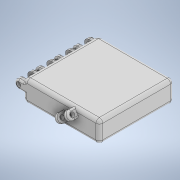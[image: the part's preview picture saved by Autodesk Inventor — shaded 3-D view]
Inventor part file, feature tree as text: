
AUTODESK INVENTOR PART (.ipt)
format: ipt  version: 2022 (Build 260153000, 153)  size: 413,696 bytes
history: native  units: mm
features: extrude x7, fillet x6, sketch x2, other x1
ambient origin geometry x8: Origin, YZ Plane, XZ Plane, XY Plane, X Axis, Y Axis, Z Axis, Center Point
bodies: Solide1 (feature_tree)
feature tree (16):
  extrude  "Extrusion1"  Depth=90.0mm
  extrude  "Extrusion5"  Depth=88.0mm
  extrude  "Extrusion6"  Depth=25.0mm TaperAngle=0.0deg
  extrude  "Extrusion7"  Depth=25.0mm
  other  "Plan de construction3"
  extrude  "Extrusion8"  Depth=22.0mm
  fillet  "Congé3"  Radius=22.0mm
  extrude  "Extrusion9"  Depth=22.0mm
  extrude  "Extrusion10"  Depth=22.0mm
  fillet  "Congé4"  Radius=2.0mm
  fillet  "Congé5"  Radius=2.0mm
  fillet  "Congé6"  Radius=2.0mm
  fillet  "Congé7"  Radius=10.0mm
  fillet  "Congé8"  Radius=5.0mm
  sketch  "Esquisse13"
  sketch  "Esquisse18"
